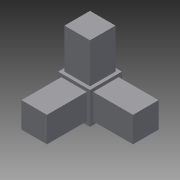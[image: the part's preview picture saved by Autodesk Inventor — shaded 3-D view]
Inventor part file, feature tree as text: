
AUTODESK INVENTOR PART (.ipt)
format: ipt  version: 2015 SP1 (Build 190203100, 203)  size: 96,768 bytes
history: native  units: mm
features: extrude x4, sketch x4
ambient origin geometry x8: Origin, YZ Plane, XZ Plane, XY Plane, X Axis, Y Axis, Z Axis, Center Point
bodies: Solid1 (feature_tree)
feature tree (8):
  extrude  "Extrusion1"  Depth=20.0mm
  extrude  "Extrusion2"  Depth=16.0mm
  extrude  "Extrusion3"  Depth=25.0mm TaperAngle=0.0deg
  extrude  "Extrusion4"  Depth=16.0mm
  sketch  "Sketch1"  dims[d0=20.0mm d1=20.0mm]
  sketch  "Sketch2"  dims[d2=20.0mm d3=0.0mm d4=16.0mm]
  sketch  "Sketch3"  dims[d5=16.0mm d6=25.0mm d7=0.0mm]
  sketch  "Sketch4"  dims[d8=16.0mm d9=16.0mm d10=25.0mm d11=0.0mm d12=16.0mm d13=16.0mm d14=25.0mm d15=0.0mm]
